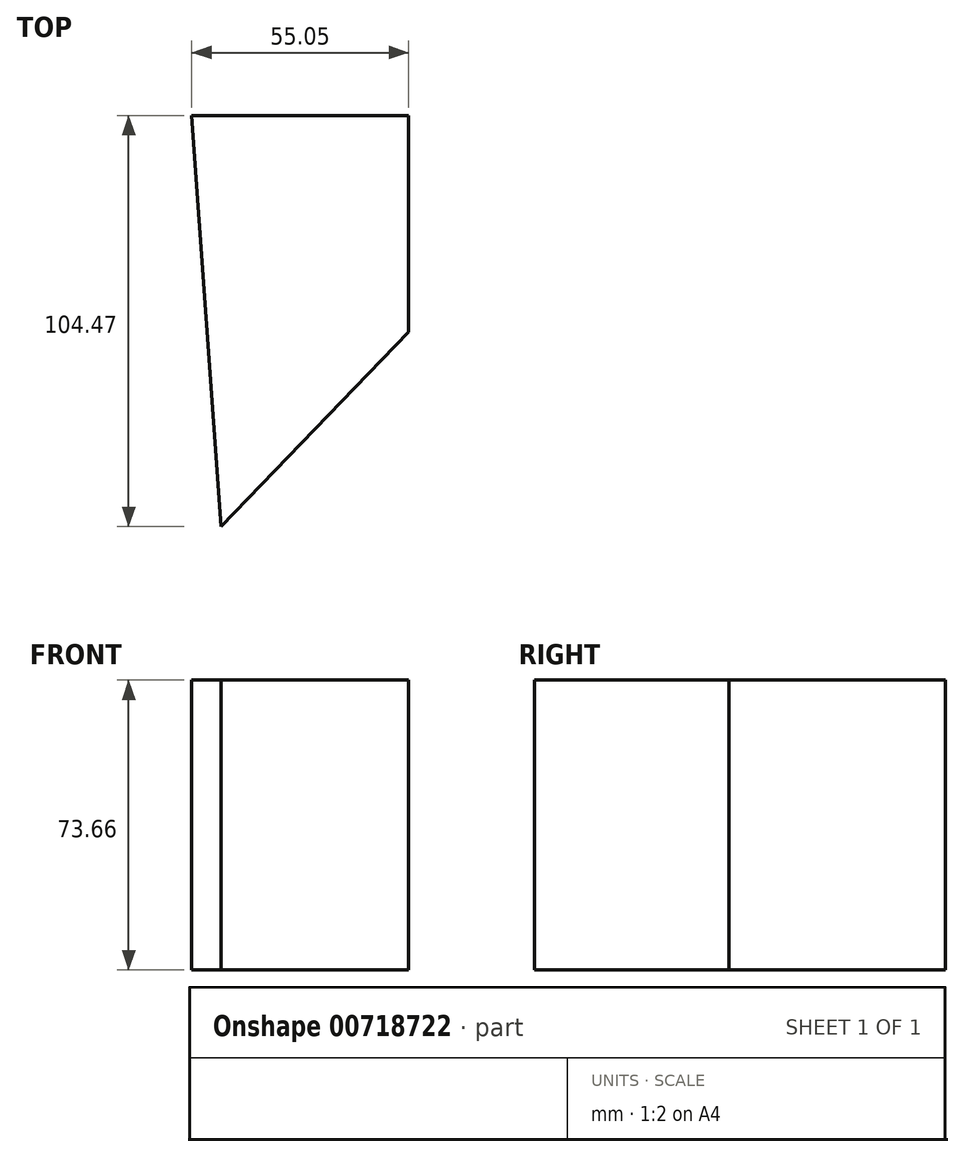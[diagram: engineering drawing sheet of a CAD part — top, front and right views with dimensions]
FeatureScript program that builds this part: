
annotation { "Feature Type Name" : "Feature", "Feature Type Description" : "" }
export const myFeature = defineFeature(function(context is Context, id is Id, definition is map)
    precondition{}
    {
        {
            var Q0;
            Q0=qCreatedBy(makeId("Top.planeOp"),FACE);
            var sketch = newSketch(context, id + "F0", { "sketchPlane" : qUnion([Q0])});
            skLineSegment(sketch, "E0", {"start": v(47.63, 0) * mm, "end": v(47.63, 55.08) * mm});
            skLineSegment(sketch, "E1", {"start": v(47.63, 55.08) * mm, "end": v(-7.42, 55.08) * mm});
            skLineSegment(sketch, "E2", {"start": v(-7.42, 55.08) * mm, "end": v(0, -49.39) * mm});
            skLineSegment(sketch, "E3", {"start": v(0, -49.39) * mm, "end": v(47.63, 0) * mm});
            skSolve(sketch);
        }
        {
            var Q0;
            Q0 = qSketchRegion(id + "F0", true);
            extrude(context, id + "F1", {"entities" : qUnion([Q0]), "oppositeDirection" : true, "depth" : 73.66 * mm, "offsetDistance" : 25.4 * mm});
        }
    });
